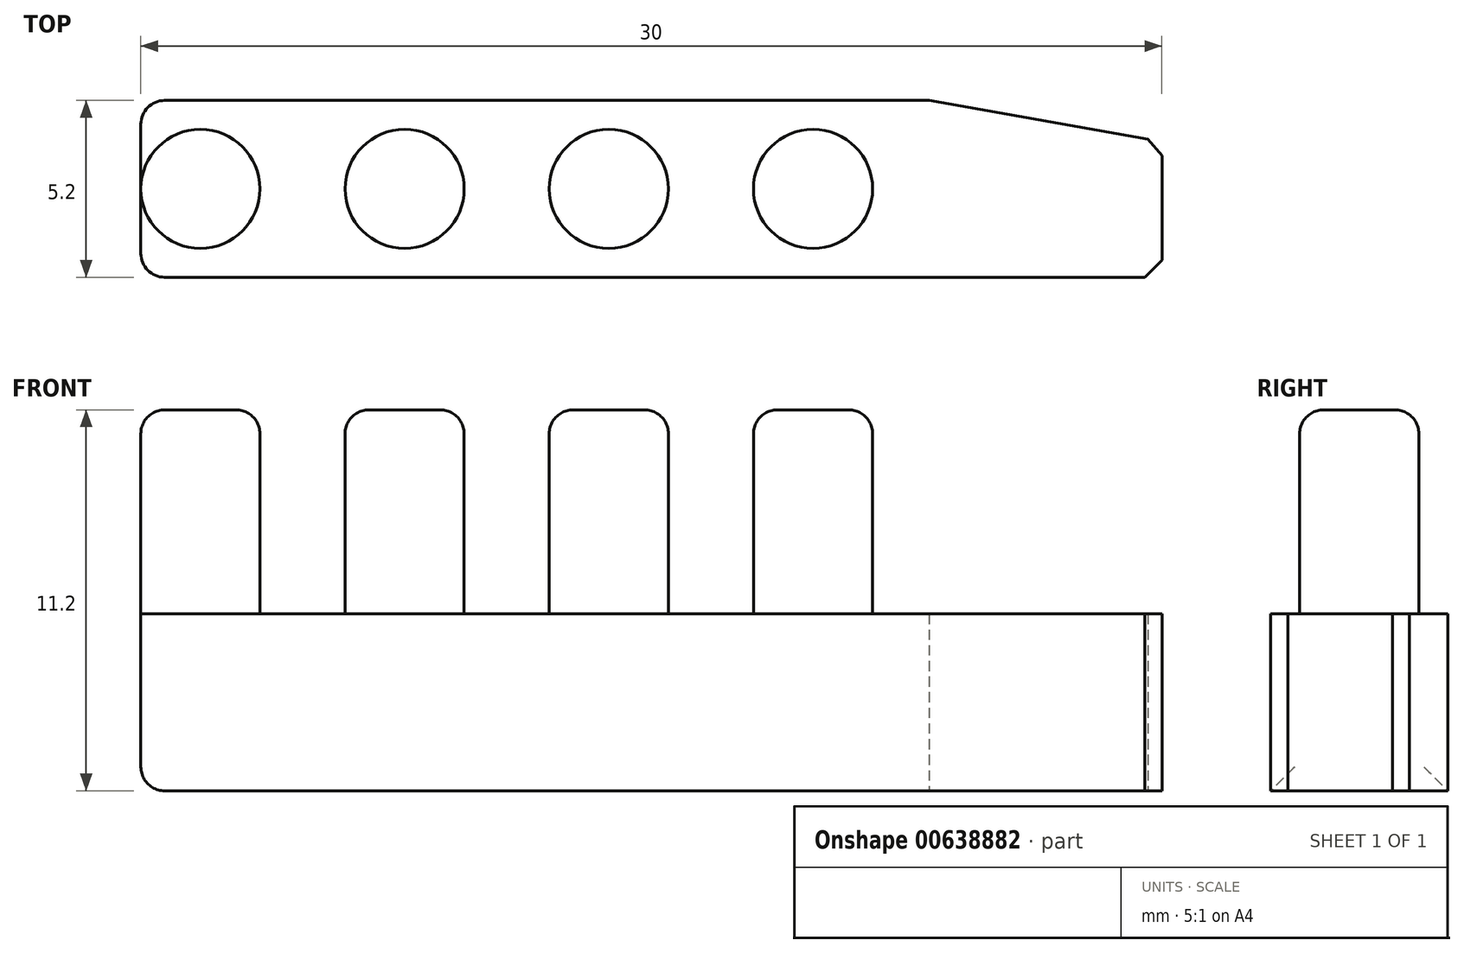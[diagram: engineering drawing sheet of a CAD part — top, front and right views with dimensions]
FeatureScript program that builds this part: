
annotation { "Feature Type Name" : "Feature", "Feature Type Description" : "" }
export const myFeature = defineFeature(function(context is Context, id is Id, definition is map)
    precondition{}
    {
        {
            var Q0;
            Q0=qCreatedBy(makeId("Top.planeOp"),FACE);
            var sketch = newSketch(context, id + "F0", { "sketchPlane" : qUnion([Q0])});
            skLineSegment(sketch, "E0.bottom", {"start": v(17.52, -2.6) * mm, "end": v(-12.48, -2.6) * mm});
            skLineSegment(sketch, "E0.top", {"start": v(17.52, 2.6) * mm, "end": v(-12.48, 2.6) * mm});
            skLineSegment(sketch, "E0.left", {"start": v(17.52, -2.6) * mm, "end": v(17.52, 2.6) * mm});
            skLineSegment(sketch, "E0.right", {"start": v(-12.48, -2.6) * mm, "end": v(-12.48, 2.6) * mm});
            skPoint(sketch, "E0.middle", {"position": v(2.52, 0) * mm});
            skLineSegment(sketch, "E1.bottom", {"start": v(-12.48, 2.6) * mm, "end": v(-5.23, 2.6) * mm, "construction": true});
            skLineSegment(sketch, "E1.top", {"start": v(-12.48, 0) * mm, "end": v(-5.23, 0) * mm, "construction": true});
            skLineSegment(sketch, "E1.left", {"start": v(-12.48, 2.6) * mm, "end": v(-12.48, 0) * mm, "construction": true});
            skLineSegment(sketch, "E2.bottom", {"start": v(-5.23, 2.6) * mm, "end": v(-1.73, 2.6) * mm, "construction": true});
            skLineSegment(sketch, "E2.top", {"start": v(-5.23, 0) * mm, "end": v(-1.73, 0) * mm, "construction": true});
            skLineSegment(sketch, "E3.bottom", {"start": v(-1.73, 2.6) * mm, "end": v(1.52, 2.6) * mm, "construction": true});
            skLineSegment(sketch, "E3.top", {"start": v(-1.73, 0) * mm, "end": v(1.52, 0) * mm, "construction": true});
            skLineSegment(sketch, "E3.right", {"start": v(1.52, 2.6) * mm, "end": v(1.52, 0) * mm, "construction": true});
            skLineSegment(sketch, "E4.bottom", {"start": v(1.52, 2.6) * mm, "end": v(17.52, 2.6) * mm, "construction": true});
            skLineSegment(sketch, "E4.top", {"start": v(1.52, 0) * mm, "end": v(17.52, 0) * mm, "construction": true});
            skLineSegment(sketch, "E4.right", {"start": v(17.52, 2.6) * mm, "end": v(17.52, 0) * mm, "construction": true});
            skLineSegment(sketch, "E5", {"start": v(17.52, -2.6) * mm, "end": v(10.68, -2.6) * mm});
            skLineSegment(sketch, "E6", {"start": v(10.68, -2.6) * mm, "end": v(17.52, -3.8) * mm});
            skLineSegment(sketch, "E7", {"start": v(17.52, -3.8) * mm, "end": v(17.52, 1.4) * mm});
            skLineSegment(sketch, "E8", {"start": v(17.52, 1.4) * mm, "end": v(10.68, 2.6) * mm});
            skLineSegment(sketch, "E9", {"start": v(10.68, 2.6) * mm, "end": v(10.68, -2.6) * mm});
            skSolve(sketch);
        }
        {
            var Q0;
            Q0=makeQuery(id+"F0.imprint","IMPRINT",FACE,{"disambiguationData":[TD([[makeQuery(id+"F0.imprint","IMPRINT",EDGE,{"derivedFrom":sQuery(id+"F0.wireOp",EDGE,"E0.bottom")}),-1.0]])]});
            var Q1;
            {var subQ0=sQuery(id+"F0.wireOp",EDGE,"E5");Q1=makeQuery(id+"F0.imprint","IMPRINT",FACE,{"disambiguationData":[TD([[makeQuery(id+"F0.imprint","IMPRINT",EDGE,{"derivedFrom":subQ0}),1.0]])]});}
            var Q2;
            {var subQ0=sQuery(id+"F0.wireOp",EDGE,"E5");Q2=makeQuery(id+"F0.imprint","IMPRINT",FACE,{"disambiguationData":[TD([[makeQuery(id+"F0.imprint","IMPRINT",EDGE,{"derivedFrom":subQ0}),-1.0]])]});}
            extrude(context, id + "F1", {"entities" : qUnion([Q0, Q1, Q2]), "depth" : 5.2 * mm, "offsetDistance" : 25 * mm});
        }
        {
            var Q0;
            Q0=makeQuery(id+"F1.opExtrude","CAP_FACE",FACE,{"disambiguationData":[OSD([sQuery(id+"F0.wireOp",EDGE,"E0.bottom"),sQuery(id+"F0.wireOp",EDGE,"E0.top"),sQuery(id+"F0.wireOp",EDGE,"E0.left"),sQuery(id+"F0.wireOp",EDGE,"E0.right")])],"isStart":false});
            var sketch = newSketch(context, id + "F2", { "sketchPlane" : qUnion([Q0])});
            skLineSegment(sketch, "E10", {"start": v(17.52, 0) * mm, "end": v(7.27, 0) * mm, "construction": true});
            skPoint(sketch, "E10.endSnap0", {"position": v(17.52, 0) * mm});
            skLineSegment(sketch, "E11", {"start": v(7.27, 0) * mm, "end": v(4.27, 0) * mm, "construction": true});
            skCircle(sketch, "E12", {"center": v(4.27, 0) * mm, "radius": 1.5 * mm, "construction": true});
            skCircle(sketch, "E13", {"center": v(7.27, 0) * mm, "radius": 1.75 * mm});
            skLineSegment(sketch, "E14", {"start": v(4.27, 0) * mm, "end": v(1.27, 0) * mm, "construction": true});
            skLineSegment(sketch, "E15", {"start": v(1.27, 0) * mm, "end": v(-1.73, 0) * mm, "construction": true});
            skLineSegment(sketch, "E16", {"start": v(-1.73, 0) * mm, "end": v(-4.73, 0) * mm, "construction": true});
            skCircle(sketch, "E17", {"center": v(1.27, 0) * mm, "radius": 1.75 * mm});
            skCircle(sketch, "E18", {"center": v(-1.73, 0) * mm, "radius": 1.5 * mm, "construction": true});
            skCircle(sketch, "E19", {"center": v(-4.73, 0) * mm, "radius": 1.75 * mm});
            skLineSegment(sketch, "E20", {"start": v(-4.73, 0) * mm, "end": v(-7.73, 0) * mm, "construction": true});
            skLineSegment(sketch, "E21", {"start": v(-7.73, 0) * mm, "end": v(-10.73, 0) * mm, "construction": true});
            skCircle(sketch, "E22", {"center": v(-10.73, 0) * mm, "radius": 1.75 * mm});
            skCircle(sketch, "E23", {"center": v(-7.73, 0) * mm, "radius": 1.5 * mm, "construction": true});
            skSolve(sketch);
        }
        {
            var Q0;
            Q0=makeQuery(id+"F2.imprint","IMPRINT",FACE,{"disambiguationData":[TD([[makeQuery(id+"F2.imprint","IMPRINT",EDGE,{"derivedFrom":sQuery(id+"F2.wireOp",EDGE,"E13")}),1.0]])]});
            var Q1;
            Q1=makeQuery(id+"F2.imprint","IMPRINT",FACE,{"disambiguationData":[TD([[makeQuery(id+"F2.imprint","IMPRINT",EDGE,{"derivedFrom":sQuery(id+"F2.wireOp",EDGE,"E17")}),1.0]])]});
            var Q2;
            {var subQ0=sQuery(id+"F2.wireOp",EDGE,"E18");var subQ1=sQuery(id+"F2.wireOp",EDGE,"E17");var subQ2=makeQuery(id+"F2.imprint","INTERSECT",VERTEX,{"disambiguationData":[OD(0.0)],"derivedFrom":[subQ1,subQ0]});Q2=makeQuery(id+"F2.imprint","IMPRINT",FACE,{"disambiguationData":[TD([[makeQuery(id+"F2.imprint","IMPRINT",EDGE,{"disambiguationData":[TD([[subQ2,-1.0]])],"derivedFrom":subQ1}),1.0]])]});}
            var Q3;
            {var subQ0=sQuery(id+"F2.wireOp",EDGE,"E19");var subQ1=makeQuery(id+"F2.imprint","INTERSECT",VERTEX,{"derivedFrom":[sQuery(id+"F2.wireOp",EDGE,"E18"),subQ0]});Q3=makeQuery(id+"F2.imprint","IMPRINT",FACE,{"disambiguationData":[TD([[makeQuery(id+"F2.imprint","IMPRINT",EDGE,{"disambiguationData":[TD([[subQ1,-1.0]])],"derivedFrom":subQ0}),1.0]])]});}
            var Q4;
            {var subQ0=sQuery(id+"F2.wireOp",EDGE,"E23");var subQ1=sQuery(id+"F2.wireOp",EDGE,"E22");var subQ2=makeQuery(id+"F2.imprint","INTERSECT",VERTEX,{"disambiguationData":[OD(0.0)],"derivedFrom":[subQ1,subQ0]});Q4=makeQuery(id+"F2.imprint","IMPRINT",FACE,{"disambiguationData":[TD([[makeQuery(id+"F2.imprint","IMPRINT",EDGE,{"disambiguationData":[TD([[subQ2,-1.0]])],"derivedFrom":subQ1}),1.0]])]});}
            var Q5;
            {var subQ0=sQuery(id+"F2.wireOp",EDGE,"E19");var subQ1=sQuery(id+"F2.wireOp",EDGE,"E18");var subQ2=makeQuery(id+"F2.imprint","INTERSECT",VERTEX,{"disambiguationData":[OD(0.0)],"derivedFrom":[subQ1,subQ0]});Q5=makeQuery(id+"F2.imprint","IMPRINT",FACE,{"disambiguationData":[TD([[makeQuery(id+"F2.imprint","IMPRINT",EDGE,{"disambiguationData":[TD([[subQ2,-1.0]])],"derivedFrom":subQ1}),-1.0]])]});}
            var Q6;
            {var subQ0=sQuery(id+"F2.wireOp",EDGE,"E17");var subQ1=sQuery(id+"F2.wireOp",EDGE,"E12");var subQ2=makeQuery(id+"F2.imprint","INTERSECT",VERTEX,{"disambiguationData":[OD(0.0)],"derivedFrom":[subQ1,subQ0]});Q6=makeQuery(id+"F2.imprint","IMPRINT",FACE,{"disambiguationData":[TD([[makeQuery(id+"F2.imprint","IMPRINT",EDGE,{"disambiguationData":[TD([[subQ2,-1.0]])],"derivedFrom":subQ1}),1.0]])]});}
            var Q7;
            Q7=makeQuery(id+"F2.imprint","IMPRINT",FACE,{"disambiguationData":[TD([[makeQuery(id+"F2.imprint","IMPRINT",EDGE,{"derivedFrom":sQuery(id+"F2.wireOp",EDGE,"E19")}),1.0]])]});
            extrude(context, id + "F3", {"entities" : qUnion([Q0, Q1, Q2, Q3, Q4, Q5, Q6, Q7]), "operationType" : NewBodyOperationType.ADD, "depth" : 6 * mm, "offsetDistance" : 25 * mm});
        }
        {
            var Q0;
            Q0=makeQuery(id+"F3.opExtrude","CAP_FACE",FACE,{"disambiguationData":[OSD([sQuery(id+"F2.wireOp",EDGE,"E12")])],"isStart":false});
            var Q1;
            Q1=makeQuery(id+"F3.opExtrude","CAP_FACE",FACE,{"disambiguationData":[OSD([sQuery(id+"F2.wireOp",EDGE,"E13")])],"isStart":false});
            var Q2;
            Q2=makeQuery(id+"F1.opExtrude","CAP_EDGE",EDGE,{"disambiguationData":[OSD([sQuery(id+"F0.wireOp",EDGE,"E0.right")])],"isStart":true});
            var Q3;
            Q3=makeQuery(id+"F3.opExtrude","CAP_FACE",FACE,{"disambiguationData":[OSD([sQuery(id+"F2.wireOp",EDGE,"E17")])],"isStart":false});
            var Q4;
            Q4=makeQuery(id+"F3.opExtrude","CAP_FACE",FACE,{"disambiguationData":[OSD([sQuery(id+"F2.wireOp",EDGE,"E18")])],"isStart":false});
            var Q5;
            Q5=makeQuery(id+"F3.opExtrude","CAP_FACE",FACE,{"disambiguationData":[OSD([sQuery(id+"F2.wireOp",EDGE,"E19")])],"isStart":false});
            var Q6;
            Q6=makeQuery(id+"F1.opExtrude","SWEPT_EDGE",EDGE,{"disambiguationData":[OSD([sQuery(id+"F0.wireOp",EDGE,"E0.top"),sQuery(id+"F0.wireOp",EDGE,"E0.right")])]});
            var Q7;
            Q7=makeQuery(id+"F1.opExtrude","SWEPT_EDGE",EDGE,{"disambiguationData":[OSD([sQuery(id+"F0.wireOp",EDGE,"E0.bottom"),sQuery(id+"F0.wireOp",EDGE,"E0.right")])]});
            var Q8;
            Q8=makeQuery(id+"F3.opExtrude","CAP_FACE",FACE,{"disambiguationData":[OSD([sQuery(id+"F2.wireOp",EDGE,"E22")])],"isStart":false});
            fillet(context, id + "F4", {"entities" : qUnion([Q0, Q1, Q2, Q3, Q4, Q5, Q6, Q7, Q8]), "radius" : .7 * mm, "tangentPropagation" : true, "allowEdgeOverflow" : false});
        }
        {
            var Q0;
            Q0=makeQuery(id+"F1.opExtrude","SWEPT_EDGE",EDGE,{"disambiguationData":[OSD([sQuery(id+"F0.wireOp",EDGE,"E0.top"),sQuery(id+"F0.wireOp",EDGE,"E0.left")])]});
            var Q1;
            Q1=makeQuery(id+"F1.opExtrude","SWEPT_EDGE",EDGE,{"disambiguationData":[OSD([sQuery(id+"F0.wireOp",EDGE,"E0.bottom"),sQuery(id+"F0.wireOp",EDGE,"E0.left")])]});
            chamfer(context, id + "F5", {"entities" : qUnion([Q0, Q1]), "width" : .5 * mm, "tangentPropagation" : true});
        }
    });
